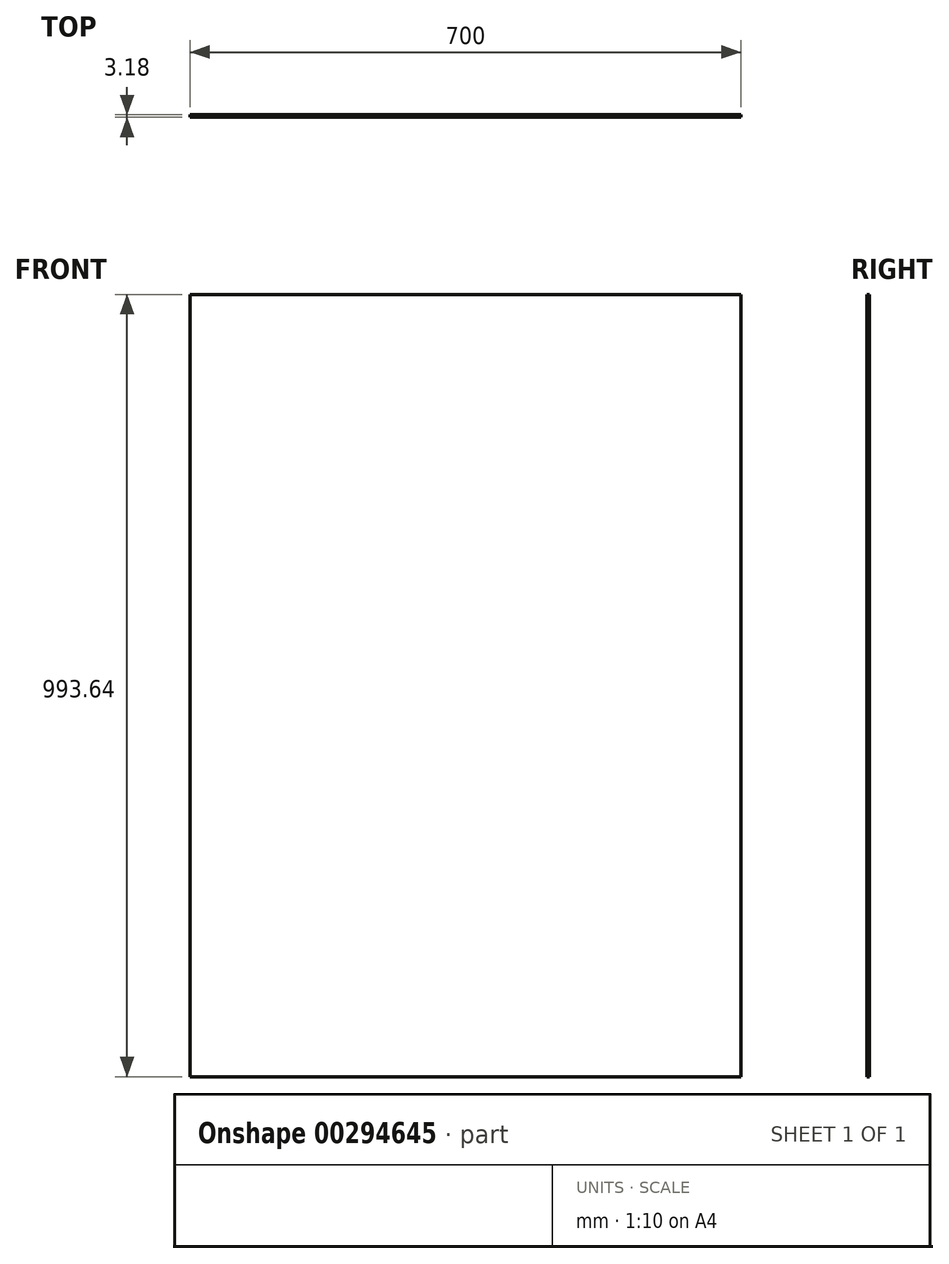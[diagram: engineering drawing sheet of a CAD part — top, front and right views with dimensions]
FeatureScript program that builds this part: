
annotation { "Feature Type Name" : "Feature", "Feature Type Description" : "" }
export const myFeature = defineFeature(function(context is Context, id is Id, definition is map)
    precondition{}
    {
        {
            var Q0;
            Q0=qCreatedBy(makeId("Front.planeOp"),FACE);
            var sketch = newSketch(context, id + "F0", { "sketchPlane" : qUnion([Q0])});
            skLineSegment(sketch, "E0.bottom", {"start": v(350, 496.82) * mm, "end": v(-350, 496.82) * mm});
            skLineSegment(sketch, "E0.top", {"start": v(350, -496.82) * mm, "end": v(-350, -496.82) * mm});
            skLineSegment(sketch, "E0.left", {"start": v(350, 496.82) * mm, "end": v(350, -496.82) * mm});
            skLineSegment(sketch, "E0.right", {"start": v(-350, 496.82) * mm, "end": v(-350, -496.82) * mm});
            skPoint(sketch, "E0.middle", {"position": v(0, 0) * mm});
            skSolve(sketch);
        }
        {
            var Q0;
            Q0 = qSketchRegion(id + "F0", true);
            extrude(context, id + "F1", {"entities" : qUnion([Q0]), "endBound" : BoundingType.SYMMETRIC, "depth" : 3.17 * mm});
        }
    });
